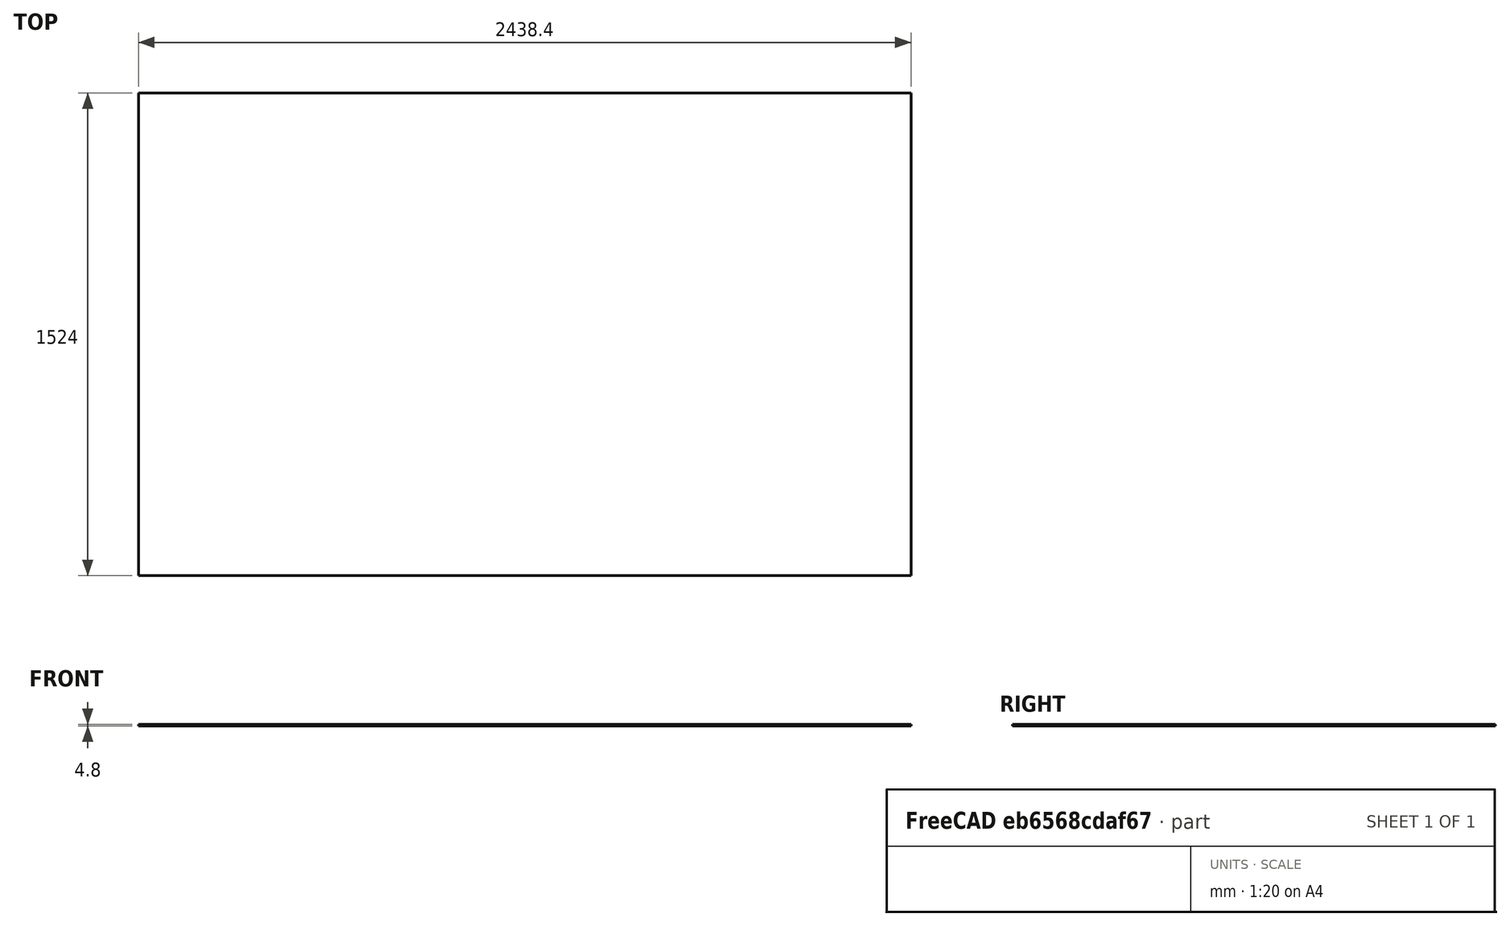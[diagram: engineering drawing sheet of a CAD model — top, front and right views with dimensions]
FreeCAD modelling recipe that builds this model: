
FCSTD DOCUMENT  (FreeCAD 1.0R38641 +468 (Git))
Label: table_5by8
License: All rights reserved
LicenseURL: https://en.wikipedia.org/wiki/All_rights_reserved
objects: PartDesign::CoordinateSystem×3, Sketcher::SketchObject×1, PartDesign::Pad×1, PartDesign::Body×1, Spreadsheet::Sheet×1, Part::FeaturePython×1, App::FeaturePython×1, App::Part×1
note: 10 computed .brp shape members not serialized (recipe doc carries the construction recipe); baked Part::Feature solids carry a one-line shape summary decoded from their .brp

FEATURE [Sketcher::SketchObject] Sketch
  ArcFitTolerance = 0
  AttachmentSupport = -> [XY_Plane]
  FullyConstrained = true
  MakeInternals = false
  MapMode = 5
  expr: Constraints[6] = Variables.width
  expr: Constraints[7] = <<dimensions>>.B2
  sketch-geometry (4):
    g0: LineSegment StartX=-1219.2 StartY=762 StartZ=0 EndX=1219.2 EndY=762 EndZ=0
    g1: LineSegment StartX=1219.2 StartY=762 StartZ=0 EndX=1219.2 EndY=-762 EndZ=0
    g2: LineSegment StartX=1219.2 StartY=-762 StartZ=0 EndX=-1219.2 EndY=-762 EndZ=0
    g3: LineSegment StartX=-1219.2 StartY=-762 StartZ=0 EndX=-1219.2 EndY=762 EndZ=0
  constraints (10):
    c: Coincident(g0,g1)
    c: Coincident(g1,g2)
    c: Coincident(g2,g3)
    c: Coincident(g3,g0)
    c: Horizontal(g2)
    c: Vertical(g1)
    c: DistanceY(g3,g3) = 1524
    c: DistanceX(g0,g0) = 2438.4
    c: Symmetric(g0,g0,g-2)
    c: Symmetric(g0,g2,g-1)
FEATURE [PartDesign::Pad] Pad  label="WorkingSurface"
  Direction = (0,0,1)
  Length = 4.8
  Length2 = 10
  Profile = -> Sketch
  ReferenceAxis = -> Sketch [N_Axis]
  Suppressed = false
  Type = 0
  expr: Length = <<dimensions>>.B3
FEATURE [PartDesign::Body] Body
  AllowCompound = false
  Group = -> [Sketch,Pad]
  Origin = -> Origin
  Tip = -> Pad
FEATURE [Spreadsheet::Sheet] Spreadsheet  label="dimensions"
  cells = A1='Width of table; B1(width)==12 * 25.4 mm * 5; C1='x_num_holes; D1==B1 / 25.4 mm - 1; A2='Length of table; B2(length)==12 * 25.4 mm * 8; C2='y_num_holes; D2==B2 / 25.4 mm - 1; A3='Table thickness; B3==4.8 mm; A4='grid offset; B4==0.5 * 25.4 mm
FEATURE [Part::FeaturePython] Facebinder  # WARN: FeaturePython — macro-defined, semantics opaque (R4)
  Area = 0
  Extrusion = 0
  RemoveSplitter = false
  Sew = false
FEATURE [PartDesign::CoordinateSystem] working_surface
  AttacherType = Attacher::AttachEngine3D
  AttachmentSupport = -> [Pad]
  MapMode = 2
FEATURE [App::FeaturePython] Variables  # WARN: FeaturePython — macro-defined, semantics opaque (R4)
  Type = App::PropertyContainer
  length = 2438.4
  width = 1524
FEATURE [PartDesign::CoordinateSystem] far_edge
  AttacherType = Attacher::AttachEngine3D
  AttachmentOffset = pos=(1219.2,0,0) rot=(0,0,1;0rad)
  AttachmentSupport = -> [Pad]
  MapMode = 2
  Placement = pos=(1219.2,0,0) rot=(0,0,1;0rad)
  expr: .AttachmentOffset.Base.x = <<dimensions>>.B2 / 2
  expr: .AttachmentOffset.Base.y = 0 mm
FEATURE [PartDesign::CoordinateSystem] close_edge
  AttacherType = Attacher::AttachEngine3D
  AttachmentOffset = pos=(-1219.2,0,0) rot=(0,0,1;0rad)
  AttachmentSupport = -> [Pad]
  MapMode = 5
  Placement = pos=(-1219.2,0,4.8) rot=(0,0,1;0rad)
  expr: .AttachmentOffset.Base.x = -<<dimensions>>.B2 / 2
FEATURE [App::Part] Part
  Group = -> [Body,working_surface,Variables,far_edge,close_edge]
  Origin = -> Origin001
